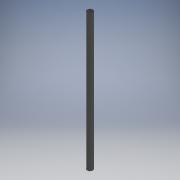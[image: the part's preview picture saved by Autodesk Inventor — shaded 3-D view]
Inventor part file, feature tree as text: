
AUTODESK INVENTOR PART (.ipt)
format: ipt  version: 2018 (Build 220112000, 112)  size: 99,328 bytes
history: native  units: mm
features: chamfer x2, extrude x1, sketch x1
ambient origin geometry x8: Origin, YZ Plane, XZ Plane, XY Plane, X Axis, Y Axis, Z Axis, Center Point
bodies: Solid1 (feature_tree)
feature tree (4):
  extrude  "Extrusion1"  Depth=1000.0mm
  chamfer  "Chamfer1"  Distance=1000.0mm
  chamfer  "Chamfer2"  Distance=1.0mm Angle=45.0deg
  sketch  "Sketch1"  dims[d0=40.0mm d1=2.0mm d2=1000.0mm d3=0.0mm d4=1.0mm d5=2.0mm d6=45.0deg d7=1.0mm d8=2.0mm d9=45.0deg]
